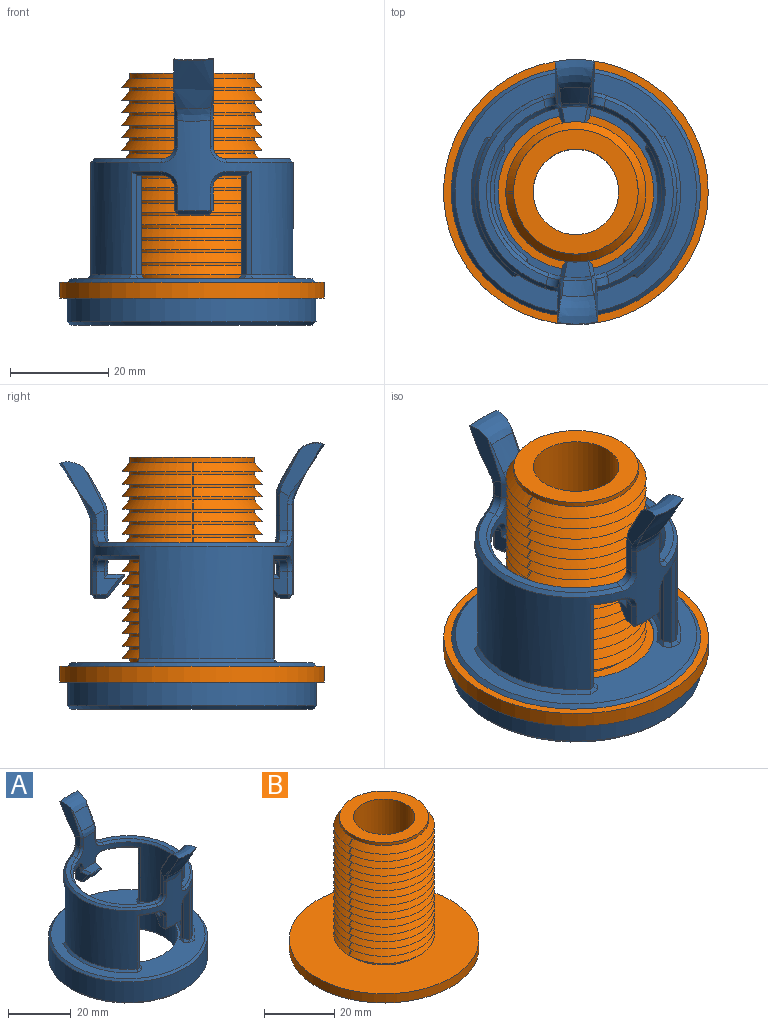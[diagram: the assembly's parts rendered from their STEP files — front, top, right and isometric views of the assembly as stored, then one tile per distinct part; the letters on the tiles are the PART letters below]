
ASSEMBLY  parts=2 mates=1
PART A: 155 faces, bbox 51.5x54.7x55.9 mm
  f0: plane 10.76x8.67mm, normal (0,0,-1), area 20.7mm2, adj f39,f47,f129,f139,f143
  f1: plane 5.56x3.84mm, normal (0,0,-1), area 8.9mm2, adj f36,f51,f82,f86,f100
  f2: plane 4.65x4.58mm, normal (-0.98,-0.2,0), area 13.4mm2, adj f45,f98,f102,f105,f106,f107
  f3: plane 4.65x4.59mm, normal (0.98,-0.19,0), area 13.4mm2, adj f47,f114,f121,f122,f126,f130
  f4: cylinder r=17.46mm len=34.93mm, axis (0,0,-1), area 1447.7mm2, adj f5,f17,f33,f34,f53,f54,f55,f56
  f5: plane 5.24x3.47mm, normal (0,0,1), area 15.2mm2, adj f4,f102,f126,f153
  f6: revolved ~5.21x4.19mm, area 24.4mm2, adj f107,f115,f122,f153
  f7: plane 6.2x2.3mm, normal (0,0,-1), area 11.8mm2, adj f106,f113,f114,f115
  f8: cylinder r=20.64mm len=41.27mm, axis (0,0,-1), area 1746.6mm2, adj f32,f35,f67,f68,f69,f70,f71,f74
  f9: plane 4.15x1.88mm, normal (-0.98,-0.2,0), area 6.3mm2, adj f22,f44,f59,f60,f66,f67
  f10: plane 4.1x1.89mm, normal (0.98,-0.19,0), area 6.2mm2, adj f24,f46,f57,f58,f78,f79
  f11: plane 37.61x14.14mm, normal (0,0,1), area 77.8mm2, adj f46,f48,f55,f76
  f12: plane 4.57x3.46mm, normal (0,0,-1), area 7.2mm2, adj f38,f50,f132,f140,f144
  f13: plane 37.7x14.14mm, normal (0,0,1), area 78.2mm2, adj f44,f49,f62,f69
  f14: plane 10.47x9.07mm, normal (0,0,-1), area 20.6mm2, adj f37,f45,f90,f93,f97
  f15: plane 6.42x1.48mm, normal (0,0,-1), area 7.3mm2, adj f108,f116,f119,f154
  f16: revolved ~5.21x3.5mm, area 20.8mm2, adj f103,f123,f152,f154
  f17: plane 5.46x3.5mm, normal (0,0,1), area 15.9mm2, adj f4,f99,f127,f152
  f18: plane 4.65x4.59mm, normal (-0.98,0.19,0), area 13.4mm2, adj f51,f95,f99,f103,f108,f109
  f19: plane 4.65x4.56mm, normal (0.98,0.21,0), area 13.4mm2, adj f50,f119,f123,f124,f127,f131
  f20: plane 8.06x1.88mm, normal (0.98,0.21,0), area 12.8mm2, adj f27,f48,f52,f53,f73,f74
  f21: plane 7.99x1.89mm, normal (-0.98,0.19,0), area 12.6mm2, adj f29,f49,f64,f65,f71,f72
  f22: plane 11.53x9.31mm, normal (-0.99,-0.15,0.09), area 35.1mm2, adj f9,f25,f31,f59,f66
  f23: extruded ~6.13x5.8mm, area 37.9mm2, adj f31,f33,f58,f59
  f24: plane 11.52x9.33mm, normal (0.99,-0.14,0.08), area 35.1mm2, adj f10,f25,f31,f58,f79
  f25: extruded ~10.1x7.97mm, area 88.6mm2, adj f22,f24,f31,f32,f66,f79
  f26: extruded ~10.13x8.22mm, area 91.7mm2, adj f27,f29,f30,f35,f72,f73
  f27: plane 11.54x9.31mm, normal (0.98,0.16,0.09), area 35.4mm2, adj f20,f26,f30,f52,f73
  f28: extruded ~6.38x5.84mm, area 39.5mm2, adj f30,f34,f52,f65
  f29: plane 11.52x9.33mm, normal (-0.99,0.14,0.08), area 35.1mm2, adj f21,f26,f30,f65,f72
  f30: bspline ~10.04x6.14mm, area 48mm2, adj f26,f27,f28,f29,f52,f65
  f31: bspline ~10.05x6.12mm, area 46.5mm2, adj f22,f23,f24,f25,f58,f59
  f32: bspline ~10.72x2.95mm, area 17.4mm2, adj f8,f25,f66,f79
  f33: bspline ~8.44x2.84mm, area 14.3mm2, adj f4,f23,f58,f59
  f34: bspline ~8.55x2.86mm, area 14.8mm2, adj f4,f28,f52,f65
  f35: bspline ~10.6x2.95mm, area 18.1mm2, adj f8,f26,f72,f73
  f36: plane 20.43x1.19mm, normal (0.71,-0.7,0), area 33.9mm2, adj f1,f82,f87,f96,f100
  f37: plane 20.54x1.28mm, normal (0.74,0.67,0), area 35.1mm2, adj f14,f84,f85,f90,f93
  f38: plane 20.37x1.3mm, normal (-0.79,-0.62,0), area 33.6mm2, adj f12,f132,f136,f144,f145
  f39: plane 20.39x1.46mm, normal (-0.47,0.88,0), area 33.6mm2, adj f0,f129,f133,f142,f143
  f40: plane 49.28x49.28mm, normal (0,0,1), area 830.2mm2, adj f43,f80,f81,f83,f84,f87,f88,f89
  f41: cylinder r=25.4mm len=50.8mm, axis (0,0,1), area 1276.9mm2, adj f149,f151
  f42: plane 49.28x49.28mm, normal (0,0,-1), area 1037.5mm2, adj f149,f150
  f43: cylinder r=15.88mm len=31.75mm, axis (0,0,-1), area 874.1mm2, adj f40,f150
  f44: cylinder r=2.54mm len=2.85mm, axis (0.2,-0.98,0), area 6.6mm2, adj f9,f13,f61,f68
  f45: cylinder r=2.54mm len=2.85mm, axis (-0.2,0.98,0), area 6.6mm2, adj f2,f14,f94,f101
  f46: cylinder r=2.54mm len=2.83mm, axis (0.19,0.98,0), area 6.6mm2, adj f10,f11,f56,f77
  f47: cylinder r=2.54mm len=2.83mm, axis (-0.19,-0.98,0), area 6.6mm2, adj f0,f3,f125,f134
  f48: cylinder r=2.54mm len=2.87mm, axis (0.21,-0.98,0), area 6.6mm2, adj f11,f20,f54,f75
  f49: cylinder r=2.54mm len=2.83mm, axis (0.19,0.98,0), area 6.6mm2, adj f13,f21,f63,f70
  f50: cylinder r=2.54mm len=2.87mm, axis (-0.21,0.98,0), area 6.6mm2, adj f12,f19,f128,f135
  f51: cylinder r=2.54mm len=2.83mm, axis (-0.19,-0.98,0), area 6.6mm2, adj f1,f18,f91,f104
  f52: bspline ~9.57x4.78mm, area 6.8mm2, adj f20,f27,f28,f30,f34,f53
  f53: plane 7.11x0.88mm, normal (0.56,0.83,0), area 7.5mm2, adj f4,f20,f52,f54
  f54: bspline ~3.33x3.31mm, area 4.9mm2, adj f4,f48,f53,f55
  f55: cone r=18.22mm half-angle=45deg, axis (0,0,1), area 47.3mm2, adj f4,f11,f54,f56
  f56: bspline ~3.33x3.31mm, area 4.9mm2, adj f4,f46,f55,f57
  f57: plane 3.16x0.85mm, normal (0.58,-0.81,0), area 3.3mm2, adj f4,f10,f56,f58
  f58: bspline ~9.71x4.91mm, area 7mm2, adj f10,f23,f24,f31,f33,f57
  f59: bspline ~9.72x4.89mm, area 7.1mm2, adj f9,f22,f23,f31,f33,f60
  f60: plane 3.2x0.87mm, normal (-0.57,-0.82,0), area 3.4mm2, adj f4,f9,f59,f61
  f61: bspline ~3.33x3.31mm, area 4.9mm2, adj f4,f44,f60,f62
  f62: cone r=18.22mm half-angle=45deg, axis (0,0,1), area 47.6mm2, adj f4,f13,f61,f63
  f63: bspline ~3.33x3.31mm, area 4.9mm2, adj f4,f49,f62,f64
  f64: plane 7.04x0.85mm, normal (-0.58,0.81,0), area 7.4mm2, adj f4,f21,f63,f65
  f65: bspline ~9.71x4.91mm, area 7mm2, adj f21,f28,f29,f30,f34,f64
  f66: bspline ~7.08x3.66mm, area 4.8mm2, adj f9,f22,f25,f32,f67
  f67: plane 1.4x0.9mm, normal (-0.82,0.57,0), area 1.5mm2, adj f8,f9,f66,f68
  f68: bspline ~3.33x3.31mm, area 5mm2, adj f8,f44,f67,f69
  f69: cone r=20.64mm half-angle=45deg, axis (0,0,-1), area 54.5mm2, adj f8,f13,f68,f70
  f70: bspline ~3.35x3.31mm, area 5mm2, adj f8,f49,f69,f71
  f71: plane 5.23x0.9mm, normal (-0.82,-0.58,0), area 5.8mm2, adj f8,f21,f70,f72
  f72: bspline ~7.3x3.8mm, area 5mm2, adj f21,f26,f29,f35,f71
  f73: bspline ~6.82x3.51mm, area 4.7mm2, adj f20,f26,f27,f35,f74
  f74: plane 5.32x0.91mm, normal (0.83,-0.56,0), area 5.8mm2, adj f8,f20,f73,f75
  f75: bspline ~3.32x3.31mm, area 5mm2, adj f8,f48,f74,f76
  f76: cone r=20.64mm half-angle=45deg, axis (0,0,-1), area 54.2mm2, adj f8,f11,f75,f77
  f77: bspline ~3.35x3.31mm, area 5mm2, adj f8,f46,f76,f78
  f78: plane 1.35x0.9mm, normal (0.82,0.58,0), area 1.5mm2, adj f8,f10,f77,f79
  f79: bspline ~7.3x3.8mm, area 5mm2, adj f10,f24,f25,f32,f78
  f80: cone r=17.46mm half-angle=45deg, axis (0,0,1), area 26.8mm2, adj f4,f40,f81,f83
  f81: plane 1.78x0.76mm, normal (0.77,0.09,0.63), area 1.3mm2, adj f40,f80,f84,f85
  f82: plane 21.1x1.16mm, normal (1,0.08,0), area 23.8mm2, adj f1,f4,f36,f83,f86
  f83: plane 2.3x0.76mm, normal (0.83,0.07,0.55), area 1.6mm2, adj f40,f80,f82,f87
  f84: plane 1.79x1.73mm, normal (0.52,0.48,0.71), area 1.9mm2, adj f37,f40,f81,f89
  f85: plane 21.1x0.91mm, normal (0.99,0.11,0), area 18.6mm2, adj f4,f37,f81,f90
  f86: cone r=17.46mm half-angle=45deg, axis (0,0,-1), area 5.6mm2, adj f1,f4,f82,f91
  f87: plane 1.72x1.71mm, normal (0.51,-0.49,0.71), area 1.8mm2, adj f36,f40,f83,f92
  f88: cone r=21.4mm half-angle=45deg, axis (0,0,-1), area 33.3mm2, adj f8,f40,f89,f92
  f89: plane 2.43x0.76mm, normal (-0.08,0.85,0.51), area 1.6mm2, adj f40,f84,f88,f93
  f90: cone r=17.46mm half-angle=45deg, axis (0,0,-1), area 13mm2, adj f4,f14,f37,f85,f94
  f91: bspline ~3.33x3.31mm, area 4.9mm2, adj f4,f51,f86,f95
  f92: plane 2x0.76mm, normal (0.06,-0.8,0.6), area 1.4mm2, adj f40,f87,f88,f96
  f93: plane 21.09x1.23mm, normal (-0.1,1,0), area 25.2mm2, adj f8,f14,f37,f89,f97
  f94: bspline ~3.33x3.31mm, area 4.9mm2, adj f4,f45,f90,f98
  f95: plane 1.28x0.85mm, normal (-0.58,0.81,0), area 1mm2, adj f4,f18,f91,f99
  f96: plane 21.1x1.02mm, normal (0.08,-1,0), area 20.8mm2, adj f8,f36,f92,f100
  f97: cone r=19.88mm half-angle=45deg, axis (0,0,1), area 14.8mm2, adj f8,f14,f93,f101
  f98: plane 1.28x0.87mm, normal (-0.57,-0.82,0), area 1mm2, adj f2,f4,f94,f102
  f99: plane 4.18x1.61mm, normal (-0.69,0.13,0.71), area 3.6mm2, adj f4,f17,f18,f95,f103,f152
  f100: cone r=19.88mm half-angle=45deg, axis (0,0,1), area 6.8mm2, adj f1,f8,f36,f96,f104
  f101: bspline ~3.33x3.31mm, area 5mm2, adj f8,f45,f97,f105
  f102: plane 4.16x1.62mm, normal (-0.69,-0.14,0.71), area 3.6mm2, adj f2,f4,f5,f98,f107,f153
  f103: bspline ~5x3.92mm, area 5.2mm2, adj f16,f18,f99,f108,f152,f154
  f104: bspline ~3.35x3.31mm, area 5mm2, adj f8,f51,f100,f109
  f105: plane 4.65x0.9mm, normal (-0.82,0.57,0), area 5.1mm2, adj f2,f8,f101,f110
  f106: plane 2.15x1.15mm, normal (-0.69,-0.14,-0.71), area 2.2mm2, adj f2,f7,f110,f111
  f107: bspline ~5.53x4.31mm, area 5.3mm2, adj f2,f6,f102,f111,f153
  f108: plane 2.46x1.16mm, normal (-0.69,0.13,-0.71), area 2.3mm2, adj f15,f18,f103,f112,f154
  f109: plane 4.65x0.9mm, normal (-0.82,-0.58,0), area 5.1mm2, adj f8,f18,f104,f112
  f110: plane 0.9x0.76mm, normal (-0.68,0.46,-0.57), area 0.5mm2, adj f105,f106,f113
  f111: plane 0.85x0.76mm, normal (-0.6,-0.43,-0.67), area 0.3mm2, adj f106,f107,f115
  f112: plane 0.9x0.76mm, normal (-0.67,-0.48,-0.57), area 0.5mm2, adj f108,f109,f116
  f113: cone r=19.88mm half-angle=45deg, axis (0,0,1), area 6.8mm2, adj f7,f8,f110,f117
  f114: plane 2.15x1.14mm, normal (0.69,-0.13,-0.71), area 2.2mm2, adj f3,f7,f117,f118
  f115: bspline ~5.39x0.84mm, area 3.6mm2, adj f6,f7,f111,f118
  f116: cone r=19.88mm half-angle=45deg, axis (0,0,1), area 7.1mm2, adj f8,f15,f112,f120
  f117: plane 0.9x0.76mm, normal (0.67,0.48,-0.57), area 0.5mm2, adj f113,f114,f121
  f118: plane 0.83x0.76mm, normal (0.61,-0.42,-0.68), area 0.3mm2, adj f114,f115,f122
  f119: plane 2.43x1.18mm, normal (0.69,0.15,-0.71), area 2.2mm2, adj f15,f19,f120,f123,f154
  f120: plane 0.91x0.76mm, normal (0.68,-0.46,-0.57), area 0.5mm2, adj f116,f119,f124
  f121: plane 4.65x0.9mm, normal (0.82,0.58,0), area 5.1mm2, adj f3,f8,f117,f125
  f122: bspline ~5.53x4.33mm, area 5.2mm2, adj f3,f6,f118,f126,f153
  f123: bspline ~5.02x3.9mm, area 5.3mm2, adj f16,f19,f119,f127,f152,f154
  f124: plane 4.65x0.91mm, normal (0.83,-0.56,0), area 5.1mm2, adj f8,f19,f120,f128
  f125: bspline ~3.35x3.31mm, area 5mm2, adj f8,f47,f121,f129
  f126: plane 4.18x1.61mm, normal (0.69,-0.13,0.71), area 3.6mm2, adj f3,f4,f5,f122,f130,f153
  f127: plane 4.14x1.67mm, normal (0.69,0.15,0.71), area 3.6mm2, adj f4,f17,f19,f123,f131,f152
  f128: bspline ~3.32x3.31mm, area 5mm2, adj f8,f50,f124,f132
  f129: cone r=19.88mm half-angle=45deg, axis (0,0,1), area 15mm2, adj f0,f8,f39,f125,f133
  f130: plane 1.28x0.85mm, normal (0.58,-0.81,0), area 1mm2, adj f3,f4,f126,f134
  f131: plane 1.28x0.88mm, normal (0.56,0.83,0), area 1mm2, adj f4,f19,f127,f135
  f132: cone r=19.88mm half-angle=45deg, axis (0,0,1), area 5.6mm2, adj f8,f12,f38,f128,f136
  f133: plane 21.1x1.02mm, normal (0.26,0.97,0), area 21.6mm2, adj f8,f39,f129,f138
  f134: bspline ~3.33x3.31mm, area 4.9mm2, adj f4,f47,f130,f139
  f135: bspline ~3.33x3.31mm, area 4.9mm2, adj f4,f50,f131,f140
  f136: plane 21.1x1.06mm, normal (-0.14,-0.99,0), area 21.9mm2, adj f8,f38,f132,f141
  f137: cone r=21.4mm half-angle=45deg, axis (0,0,-1), area 34mm2, adj f8,f40,f138,f141
  f138: plane 2.01x0.95mm, normal (0.21,0.78,0.59), area 1.5mm2, adj f40,f133,f137,f142
  f139: cone r=17.46mm half-angle=45deg, axis (0,0,-1), area 12.9mm2, adj f0,f4,f134,f143
  f140: cone r=17.46mm half-angle=45deg, axis (0,0,-1), area 4.6mm2, adj f4,f12,f135,f144
  f141: plane 2.09x0.76mm, normal (-0.11,-0.8,0.58), area 1.5mm2, adj f40,f136,f137,f145
  f142: plane 1.82x1.45mm, normal (-0.33,0.63,0.71), area 1.8mm2, adj f39,f40,f138,f146
  f143: plane 21.1x1.1mm, normal (-0.97,0.26,0), area 23.1mm2, adj f0,f4,f39,f139,f146
  f144: plane 21.1x1.11mm, normal (-0.99,0.14,0), area 22.8mm2, adj f4,f12,f38,f140,f147
  f145: plane 1.77x1.62mm, normal (-0.56,-0.44,0.71), area 1.8mm2, adj f38,f40,f141,f147
  f146: plane 2.16x0.94mm, normal (-0.8,0.21,0.56), area 1.5mm2, adj f40,f142,f143,f148
  f147: plane 2.18x0.76mm, normal (-0.81,0.12,0.57), area 1.5mm2, adj f40,f144,f145,f148
  f148: cone r=17.46mm half-angle=45deg, axis (0,0,1), area 27.8mm2, adj f4,f40,f146,f147
  f149: cone r=24.64mm half-angle=45deg, axis (0,0,1), area 169.4mm2, adj f41,f42
  f150: cone r=15.88mm half-angle=45deg, axis (0,0,-1), area 110.1mm2, adj f42,f43
  f151: cone r=25.4mm half-angle=45deg, axis (0,0,-1), area 169.4mm2, adj f40,f41
  f152: bspline ~5.32x0.83mm, area 2.4mm2, adj f16,f17,f99,f103,f123,f127
  f153: bspline ~5.32x0.81mm, area 2.3mm2, adj f5,f6,f102,f107,f122,f126
  f154: bspline ~10.37x2.76mm, area 13.5mm2, adj f15,f16,f103,f108,f119,f123
PART B: 70 faces, bbox 54x54x45.8 mm
  f0: plane 28.6x28.6mm, normal (0,0,-1), area 134.6mm2, adj f1,f2,f3
  f1: plane 1.91x1.59mm, normal (-0.77,0,0.64), area 0.6mm2, adj f0,f2,f59
  f2: revolved ~28.58x28.58mm, area 209.8mm2, adj f0,f1,f59
  f3: cylinder r=12.7mm len=25.4mm, axis (0,0,-1), area 50.6mm2, adj f0,f29,f30
  f4: plane 28.6x28.6mm, normal (0,0,-1), area 134.6mm2, adj f5,f6,f7
  f5: plane 1.91x1.59mm, normal (-0.77,0,0.64), area 0.6mm2, adj f4,f6,f15
  f6: revolved ~28.58x28.58mm, area 209.8mm2, adj f4,f5,f15
  f7: cylinder r=12.7mm len=25.4mm, axis (0,0,-1), area 50.6mm2, adj f4,f21,f22
  f8: plane 28.6x28.6mm, normal (0,0,-1), area 134.6mm2, adj f9,f10,f11
  f9: plane 1.91x1.59mm, normal (-0.77,0,0.64), area 0.6mm2, adj f8,f10,f63
  f10: revolved ~28.58x28.58mm, area 209.8mm2, adj f8,f9,f63
  f11: cylinder r=12.7mm len=25.4mm, axis (0,0,-1), area 50.6mm2, adj f8,f13,f14
  f12: plane 28.6x28.6mm, normal (0,0,-1), area 134.6mm2, adj f13,f14,f15
  f13: plane 1.91x1.59mm, normal (-0.77,0,0.64), area 0.6mm2, adj f11,f12,f14
  f14: revolved ~28.58x28.58mm, area 209.8mm2, adj f11,f12,f13
  f15: cylinder r=12.7mm len=25.4mm, axis (0,0,-1), area 50.6mm2, adj f5,f6,f12
  f16: plane 28.6x28.6mm, normal (0,0,-1), area 134.6mm2, adj f17,f18,f19
  f17: plane 1.91x1.59mm, normal (-0.77,0,0.64), area 0.6mm2, adj f16,f18,f43
  f18: revolved ~28.58x28.58mm, area 209.8mm2, adj f16,f17,f43
  f19: cylinder r=12.7mm len=25.4mm, axis (0,0,-1), area 50.6mm2, adj f16,f61,f62
  f20: plane 28.6x28.6mm, normal (0,0,-1), area 134.6mm2, adj f21,f22,f23
  f21: plane 1.91x1.59mm, normal (-0.77,0,0.64), area 0.6mm2, adj f7,f20,f22
  f22: revolved ~28.58x28.58mm, area 209.8mm2, adj f7,f20,f21
  f23: cylinder r=12.7mm len=25.4mm, axis (0,0,-1), area 50.6mm2, adj f20,f37,f38
  f24: plane 28.6x28.6mm, normal (0,0,-1), area 134.6mm2, adj f25,f26,f27
  f25: plane 1.91x1.59mm, normal (-0.77,0,0.64), area 0.6mm2, adj f24,f26,f35
  f26: revolved ~28.58x28.58mm, area 209.8mm2, adj f24,f25,f35
  f27: cylinder r=12.7mm len=25.4mm, axis (0,0,-1), area 50.6mm2, adj f24,f57,f58
  f28: plane 28.6x28.6mm, normal (0,0,-1), area 134.6mm2, adj f29,f30,f31
  f29: plane 1.91x1.59mm, normal (-0.77,0,0.64), area 0.6mm2, adj f3,f28,f30
  f30: revolved ~28.58x28.58mm, area 209.8mm2, adj f3,f28,f29
  f31: cylinder r=12.7mm len=25.4mm, axis (0,0,-1), area 50.6mm2, adj f28,f53,f54
  f32: plane 28.6x28.6mm, normal (0,0,-1), area 134.6mm2, adj f33,f34,f35
  f33: plane 1.91x1.59mm, normal (-0.77,0,0.64), area 0.6mm2, adj f32,f34,f39
  f34: revolved ~28.58x28.58mm, area 209.8mm2, adj f32,f33,f39
  f35: cylinder r=12.7mm len=25.4mm, axis (0,0,-1), area 50.6mm2, adj f25,f26,f32
  f36: plane 28.6x28.6mm, normal (0,0,-1), area 134.6mm2, adj f37,f38,f39
  f37: plane 1.91x1.59mm, normal (-0.77,0,0.64), area 0.6mm2, adj f23,f36,f38
  f38: revolved ~28.58x28.58mm, area 209.8mm2, adj f23,f36,f37
  f39: cylinder r=12.7mm len=25.4mm, axis (0,0,-1), area 50.6mm2, adj f33,f34,f36
  f40: plane 28.6x28.6mm, normal (0,0,-1), area 134.6mm2, adj f41,f42,f43
  f41: plane 1.91x1.59mm, normal (-0.77,0,0.64), area 0.6mm2, adj f40,f42,f47
  f42: revolved ~28.58x28.58mm, area 209.8mm2, adj f40,f41,f47
  f43: cylinder r=12.7mm len=25.4mm, axis (0,0,-1), area 50.6mm2, adj f17,f18,f40
  f44: plane 28.6x28.6mm, normal (0,0,-1), area 134.6mm2, adj f45,f46,f47
  f45: plane 1.91x1.59mm, normal (-0.77,0,0.64), area 0.6mm2, adj f44,f46,f51
  f46: revolved ~28.58x28.58mm, area 209.8mm2, adj f44,f45,f51
  f47: cylinder r=12.7mm len=25.4mm, axis (0,0,-1), area 50.6mm2, adj f41,f42,f44
  f48: plane 28.6x28.6mm, normal (0,0,-1), area 134.6mm2, adj f49,f50,f51
  f49: plane 1.91x1.59mm, normal (-0.77,0,0.64), area 0.6mm2, adj f48,f50,f67
  f50: revolved ~28.58x28.58mm, area 209.8mm2, adj f48,f49,f67
  f51: cylinder r=12.7mm len=25.4mm, axis (0,0,-1), area 50.6mm2, adj f45,f46,f48
  f52: plane 28.6x28.6mm, normal (0,0,-1), area 134.6mm2, adj f53,f54,f55
  f53: plane 1.91x1.59mm, normal (-0.77,0,0.64), area 0.6mm2, adj f31,f52,f54
  f54: revolved ~28.58x28.58mm, area 209.8mm2, adj f31,f52,f53
  f55: cylinder r=12.7mm len=25.4mm, axis (0,0,-1), area 125.5mm2, adj f52,f66
  f56: plane 28.6x28.6mm, normal (0,0,-1), area 134.6mm2, adj f57,f58,f59
  f57: plane 1.91x1.59mm, normal (-0.77,0,0.64), area 0.6mm2, adj f27,f56,f58
  f58: revolved ~28.58x28.58mm, area 209.8mm2, adj f27,f56,f57
  f59: cylinder r=12.7mm len=25.4mm, axis (0,0,-1), area 50.6mm2, adj f1,f2,f56
  f60: plane 28.6x28.6mm, normal (0,0,-1), area 134.6mm2, adj f61,f62,f63
  f61: plane 1.91x1.59mm, normal (-0.77,0,0.64), area 0.6mm2, adj f19,f60,f62
  f62: revolved ~28.58x28.58mm, area 209.8mm2, adj f19,f60,f61
  f63: cylinder r=12.7mm len=25.4mm, axis (0,0,-1), area 50.6mm2, adj f9,f10,f60
  f64: cylinder r=26.99mm len=53.98mm, axis (0,0,1), area 538.4mm2, adj f65,f66
  f65: plane 53.98x53.98mm, normal (0,0,-1), area 2048.6mm2, adj f64,f69
  f66: plane 53.98x53.98mm, normal (0,0,1), area 1781.4mm2, adj f55,f64
  f67: cylinder r=12.7mm len=25.4mm, axis (0,0,-1), area 83.2mm2, adj f49,f50,f68
  f68: plane 25.4x25.4mm, normal (0,0,1), area 267.2mm2, adj f67,f69
  f69: cylinder r=8.73mm len=45.8mm, axis (0,0,1), area 2512.4mm2, adj f65,f68
PLACE A t=(15.1,-25.08,17.59)mm
PLACE B t=(14.88,-7.62,-1.19)mm
MATE slider A.f4 <-> B.f64  axis (0,0,-1) through (14.88,-7.62,-1.19)mm
